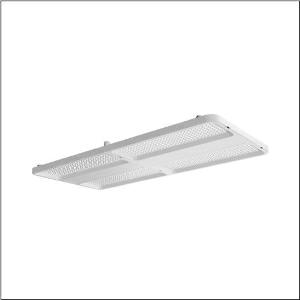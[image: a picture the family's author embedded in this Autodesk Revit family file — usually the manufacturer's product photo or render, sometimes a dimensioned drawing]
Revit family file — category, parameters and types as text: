
# Revit family: highbay_21_maxi_52hn12db4wda
name_source: partatom
category: Lighting Fixtures
units: mm (PartAtom-declared; Revit-internal decimal feet)

## family parameters
Cut with Voids When Loaded = No
Host = Face
Light Source = No
Part Type = Normal
Room Calculation Point = No
Round Connector Dimension = Use Diameter
Shared = No

## types (1)
- --- (1 x LED, 10140 lm, 55.2 W, 4000K)
    Apparent Load = 55 VA
    CIE Flux Codes = 90 98 100 100 100
    Color Rendering = 80
    Color Temperature = 4000K
    Default Elevation = 1800 mm
    Description = high bay luminaire Highbay 21 maxi; direct symmetric wide distribution, light control with lens of PMMA; UGR ≤ 22 (X = 4H | Y = 8H | S = 0.25H | reflection values 70/50/20); luminous flux: 64.000lm; light colour: 840, colour temperature: 4000K, MacAdam ≤ 3 SDCM (initial), colour rendering: CRI > 80; luminous efficacy: 185,5lm/W; rated service life: 75.000h (L80) at AT= ta max; control: DALI 2; luminaire connection: terminal, 5-pole, max. 2.5mm² (cable entry for one cable, Ø 8.5..16mm); mains connection: 230..240V, AC/DC 0/50..60Hz; connected load: 345W; protection rating (complete): IP66; insulation class (complete): insulation class I (protective earthing); protection symbol: D; impact resistance: IK08; certification: CE, ENEC, VDE, UKCA; luminaire for central battery installations according to EN 60598-2-22, internal wiring halogen-free; luminaire LABS conformity tested according to VDMA 24364:2018-05; Suitable for use in the food industry according to the specifications of IFS-Food, HACCP and/or BRC; housing frame of high-performance plastic PA6, matt traffic white (RAL 9016); cover of PMMA; dimension (LxWxH): 946 x 442 x 72mm; permissible operating ambient temperature: -40..+50°C (reducing of maximum allowable ambient temperature of 5°C with ceiling mounting); packaging unit: 1 piece; (delivery without accessories; please order mounting accessories separately)
    Height = 72 mm  [stored 0.23622 ft]
    Lamp = 1 x LED
    Lamp Light Flux = 10140 lm
    Lamp Power = 55.2 W
    Lamp count = 1
    Length = 946 mm
    Luminous efficacy = 184 lm/W
    Manufacturer = Siteco
    ModVariant = No
    Model = 52HN12DB4WDA
    Mounting Place = Ceiling
    Mounting Type = Pendant
    Number of Poles = 1
    OnlyDefault = Yes
    Power Factor = 1
    Product Name = Highbay 21 maxi
    Product group = high bay luminaire
    ProductGroupID = 902
    Protection Class = Protection class I
    Protection Degree = IP 66
    RLX_Detail_Level = 1
    RLX_Emergency_Light_Flux = 0 lm
    RLX_Emergency_Type = 0
    RLX_Emergency_Type_DB = No
    RlxData = <blob elided: 128473 chars, md5=d79b713b>
    Socket = socket
    Standby Power = 0 W
    System Light Flux = 10140 lm
    System Power = 55 W
    Type Comments = : DC mode (central or group accumulator) initial emergency light level
    Type Image = l_1363244.jpg
    URL = http://relux.com
    VarID = @adj_019265
    Voltage = 0 V
    Weight = 0.00 kg
    Width = 442 mm

note: [stored X ft] marks values corroborated as IEEE doubles in the binary element streams (Revit-internal decimal feet)

## geometry (parser evidence)
native form markers: Blend x4, Sweep x11
no freeform markers — native parametric forms only
